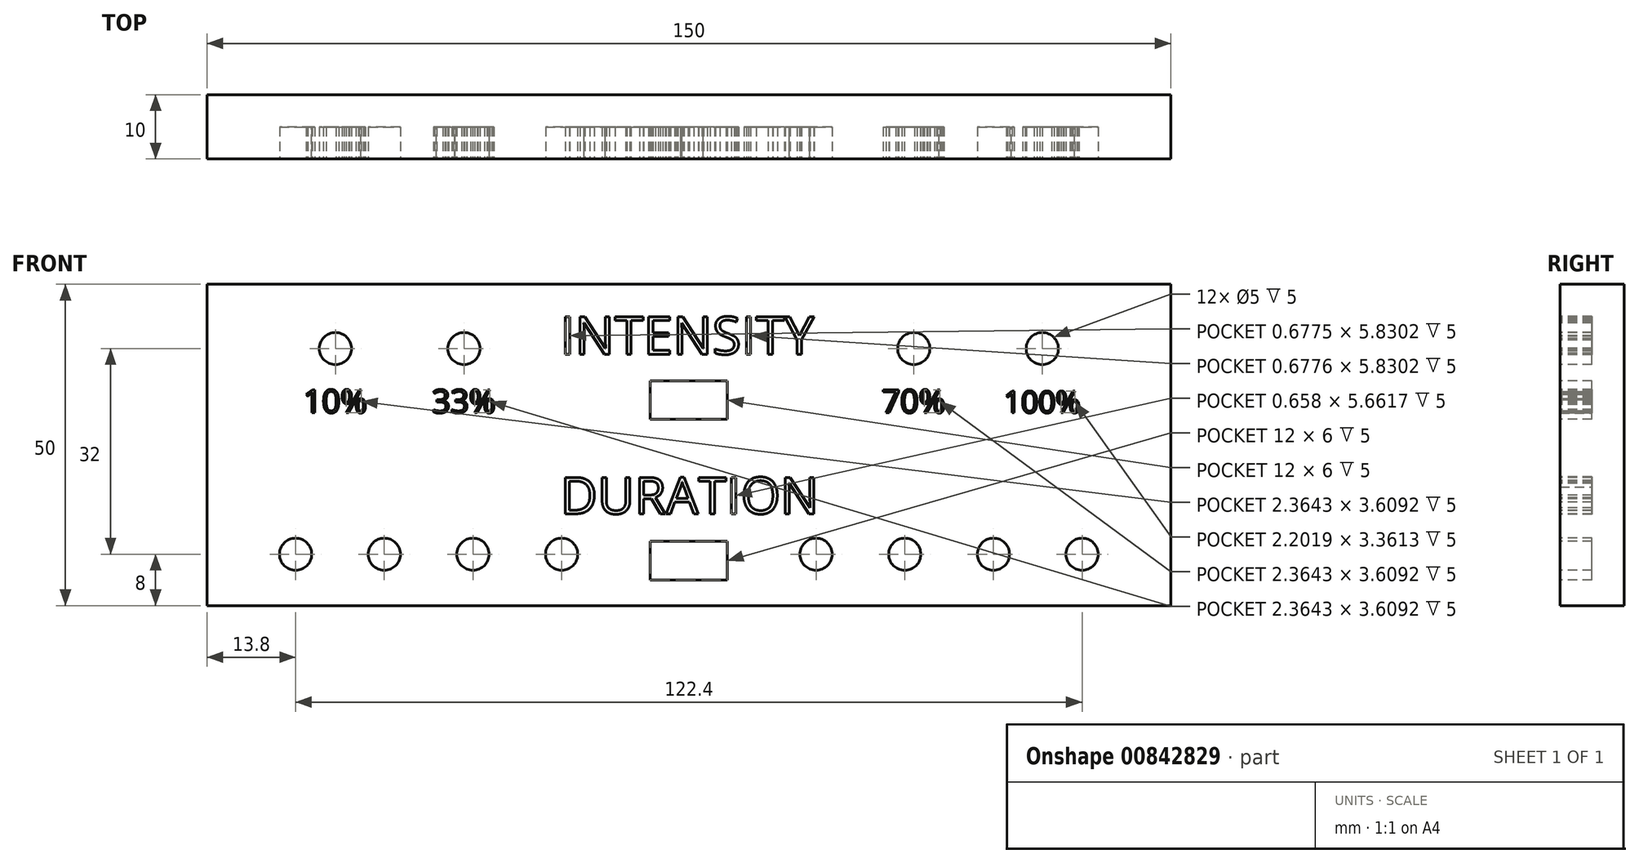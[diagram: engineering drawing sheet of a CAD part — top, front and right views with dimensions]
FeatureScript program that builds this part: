
annotation { "Feature Type Name" : "Feature", "Feature Type Description" : "" }
export const myFeature = defineFeature(function(context is Context, id is Id, definition is map)
    precondition{}
    {
        {
            var Q0;
            Q0=qCreatedBy(makeId("Front.planeOp"),FACE);
            var sketch = newSketch(context, id + "F0", { "sketchPlane" : qUnion([Q0])});
            skLineSegment(sketch, "E0.bottom", {"start": v(75, -25) * mm, "end": v(-75, -25) * mm});
            skLineSegment(sketch, "E0.top", {"start": v(75, 25) * mm, "end": v(-75, 25) * mm});
            skLineSegment(sketch, "E0.left", {"start": v(75, -25) * mm, "end": v(75, 25) * mm});
            skLineSegment(sketch, "E0.right", {"start": v(-75, -25) * mm, "end": v(-75, 25) * mm});
            skPoint(sketch, "E0.middle", {"position": v(0, 0) * mm});
            skSolve(sketch);
        }
        {
            var Q0;
            Q0=makeQuery(id+"F0.imprint","IMPRINT",FACE,{"disambiguationData":[TD([[makeQuery(id+"F0.imprint","IMPRINT",EDGE,{"derivedFrom":sQuery(id+"F0.wireOp",EDGE,"E0.bottom")}),-1.0]])]});
            extrude(context, id + "F1", {"entities" : qUnion([Q0]), "depth" : 10 * mm, "offsetDistance" : 25 * mm});
        }
        {
            var Q0;
            Q0=makeQuery(id+"F1.opExtrude","CAP_FACE",FACE,{"disambiguationData":[OSD([sQuery(id+"F0.wireOp",EDGE,"E0.bottom"),sQuery(id+"F0.wireOp",EDGE,"E0.top"),sQuery(id+"F0.wireOp",EDGE,"E0.left"),sQuery(id+"F0.wireOp",EDGE,"E0.right")])],"isStart":false});
            var sketch = newSketch(context, id + "F2", { "sketchPlane" : qUnion([Q0])});
            skText(sketch, "E1", { "text": "INTENSITY", "fontName": "OpenSans-Regular.ttf"});
            skText(sketch, "E2", { "text": "DURATION", "fontName": "OpenSans-Regular.ttf"});
            const initialGuessF2  = {"E1": [-0.02, 0.01412, 1, 0, 0.00588], "E2": [-0.02, -0.01071, 1, 0, 0.00571]};
            skSetInitialGuess(sketch, initialGuessF2);
            skSolve(sketch);
        }
        {
            var Q0;
            Q0 = qSketchRegion(id + "F2", true);
            extrude(context, id + "F3", {"entities" : qUnion([Q0]), "operationType" : NewBodyOperationType.REMOVE, "oppositeDirection" : true, "depth" : 5 * mm, "offsetDistance" : 25 * mm});
        }
        {
            var Q0;
            {var subQ0=sQuery(id+"F0.wireOp",EDGE,"E0.top");var subQ1=sQuery(id+"F0.wireOp",EDGE,"E0.right");var subQ2=sQuery(id+"F0.wireOp",EDGE,"E0.bottom");var subQ3=sQuery(id+"F0.wireOp",EDGE,"E0.left");Q0=makeQuery(id+"F3.boolean.opBoolean","SPLIT",FACE,{"disambiguationData":[TD([makeQuery(id+"F1.opExtrude","SWEPT_FACE",FACE,{"disambiguationData":[OSD([subQ2])]})])],"derivedFrom":makeQuery(id+"F1.opExtrude","CAP_FACE",FACE,{"disambiguationData":[OSD([subQ2,subQ0,subQ3,subQ1])],"isStart":false})});}
            var sketch = newSketch(context, id + "F4", { "sketchPlane" : qUnion([Q0])});
            skLineSegment(sketch, "E3.bottom", {"start": v(6, 4) * mm, "end": v(-6, 4) * mm});
            skLineSegment(sketch, "E3.top", {"start": v(6, 10) * mm, "end": v(-6, 10) * mm});
            skLineSegment(sketch, "E3.left", {"start": v(6, 4) * mm, "end": v(6, 10) * mm});
            skLineSegment(sketch, "E3.right", {"start": v(-6, 4) * mm, "end": v(-6, 10) * mm});
            skPoint(sketch, "E3.middle", {"position": v(0, 7) * mm});
            skLineSegment(sketch, "E4.bottom", {"start": v(6, -21) * mm, "end": v(-6, -21) * mm});
            skLineSegment(sketch, "E4.top", {"start": v(6, -15) * mm, "end": v(-6, -15) * mm});
            skLineSegment(sketch, "E4.left", {"start": v(6, -21) * mm, "end": v(6, -15) * mm});
            skLineSegment(sketch, "E4.right", {"start": v(-6, -21) * mm, "end": v(-6, -15) * mm});
            skPoint(sketch, "E4.middle", {"position": v(0, -18) * mm});
            skSolve(sketch);
        }
        {
            var Q0;
            Q0 = qSketchRegion(id + "F4", true);
            extrude(context, id + "F5", {"entities" : qUnion([Q0]), "operationType" : NewBodyOperationType.REMOVE, "oppositeDirection" : true, "depth" : 5 * mm, "offsetDistance" : 25 * mm});
        }
        {
            var Q0;
            {var subQ0=sQuery(id+"F0.wireOp",EDGE,"E0.top");var subQ1=sQuery(id+"F0.wireOp",EDGE,"E0.right");var subQ2=sQuery(id+"F0.wireOp",EDGE,"E0.bottom");var subQ3=sQuery(id+"F0.wireOp",EDGE,"E0.left");Q0=makeQuery(id+"F3.boolean.opBoolean","SPLIT",FACE,{"disambiguationData":[TD([makeQuery(id+"F1.opExtrude","SWEPT_FACE",FACE,{"disambiguationData":[OSD([subQ2])]})])],"derivedFrom":makeQuery(id+"F1.opExtrude","CAP_FACE",FACE,{"disambiguationData":[OSD([subQ2,subQ0,subQ3,subQ1])],"isStart":false})});}
            var sketch = newSketch(context, id + "F6", { "sketchPlane" : qUnion([Q0])});
            skCircle(sketch, "E5", {"center": v(-55, 15) * mm, "radius": 2.5 * mm});
            skPoint(sketch, "E6.centerSnap0", {"position": v(12.3, 16.74) * mm});
            skCircle(sketch, "E7", {"center": v(35, 15) * mm, "radius": 2.5 * mm});
            skCircle(sketch, "E8", {"center": v(-35, 15) * mm, "radius": 2.5 * mm});
            skCircle(sketch, "E9", {"center": v(55, 15) * mm, "radius": 2.5 * mm});
            skSolve(sketch);
        }
        {
            var Q0;
            Q0=makeQuery(id+"F6.imprint","IMPRINT",FACE,{"disambiguationData":[TD([[makeQuery(id+"F6.imprint","IMPRINT",EDGE,{"derivedFrom":sQuery(id+"F6.wireOp",EDGE,"E5")}),1.0]])]});
            var Q1;
            Q1=makeQuery(id+"F6.imprint","IMPRINT",FACE,{"disambiguationData":[TD([[makeQuery(id+"F6.imprint","IMPRINT",EDGE,{"derivedFrom":sQuery(id+"F6.wireOp",EDGE,"E8")}),1.0]])]});
            var Q2;
            Q2=makeQuery(id+"F6.imprint","IMPRINT",FACE,{"disambiguationData":[TD([[makeQuery(id+"F6.imprint","IMPRINT",EDGE,{"derivedFrom":sQuery(id+"F6.wireOp",EDGE,"E7")}),1.0]])]});
            var Q3;
            Q3=makeQuery(id+"F6.imprint","IMPRINT",FACE,{"disambiguationData":[TD([[makeQuery(id+"F6.imprint","IMPRINT",EDGE,{"derivedFrom":sQuery(id+"F6.wireOp",EDGE,"E9")}),1.0]])]});
            extrude(context, id + "F7", {"entities" : qUnion([Q0, Q1, Q2, Q3]), "operationType" : NewBodyOperationType.REMOVE, "oppositeDirection" : true, "depth" : 5 * mm, "offsetDistance" : 25 * mm});
        }
        {
            var Q0;
            {var subQ0=sQuery(id+"F0.wireOp",EDGE,"E0.top");var subQ1=sQuery(id+"F0.wireOp",EDGE,"E0.right");var subQ2=sQuery(id+"F0.wireOp",EDGE,"E0.bottom");var subQ3=sQuery(id+"F0.wireOp",EDGE,"E0.left");Q0=makeQuery(id+"F3.boolean.opBoolean","SPLIT",FACE,{"disambiguationData":[TD([makeQuery(id+"F1.opExtrude","SWEPT_FACE",FACE,{"disambiguationData":[OSD([subQ2])]})])],"derivedFrom":makeQuery(id+"F1.opExtrude","CAP_FACE",FACE,{"disambiguationData":[OSD([subQ2,subQ0,subQ3,subQ1])],"isStart":false})});}
            var sketch = newSketch(context, id + "F8", { "sketchPlane" : qUnion([Q0])});
            skText(sketch, "E10", { "text": "33%", "fontName": "OpenSans-Regular.ttf"});
            skText(sketch, "E11", { "text": "70%", "fontName": "OpenSans-Regular.ttf"});
            skText(sketch, "E12", { "text": "100%", "fontName": "OpenSans-Regular.ttf"});
            skText(sketch, "E13", { "text": "10%", "fontName": "OpenSans-Regular.ttf"});
            const initialGuessF8  = {"E10": [-0.04, 0.005, 1, 0, 0.00364], "E11": [0.03, 0.005, 1, 0, 0.00364], "E12": [0.049, 0.005, 1, 0, 0.00339], "E13": [-0.06, 0.005, 1, 0, 0.00364]};
            skSetInitialGuess(sketch, initialGuessF8);
            skSolve(sketch);
        }
        {
            var Q0;
            Q0 = qSketchRegion(id + "F8", true);
            extrude(context, id + "F9", {"entities" : qUnion([Q0]), "operationType" : NewBodyOperationType.REMOVE, "oppositeDirection" : true, "depth" : 5 * mm, "offsetDistance" : 25 * mm});
        }
        {
            var Q0;
            {var subQ98=sQuery(id+"F0.wireOp",EDGE,"E0.bottom");var subQ99=makeQuery(id+"F1.opExtrude","SWEPT_FACE",FACE,{"disambiguationData":[OSD([subQ98])]});var subQ107=sQuery(id+"F0.wireOp",EDGE,"E0.right");var subQ114=sQuery(id+"F0.wireOp",EDGE,"E0.top");var subQ120=sQuery(id+"F0.wireOp",EDGE,"E0.left");Q0=makeQuery(id+"F9.boolean.opBoolean","SPLIT",FACE,{"disambiguationData":[TD([subQ99])],"derivedFrom":makeQuery(id+"F3.boolean.opBoolean","SPLIT",FACE,{"disambiguationData":[TD([subQ99])],"derivedFrom":makeQuery(id+"F1.opExtrude","CAP_FACE",FACE,{"disambiguationData":[OSD([subQ98,subQ114,subQ120,subQ107])],"isStart":false})})});}
            var sketch = newSketch(context, id + "F10", { "sketchPlane" : qUnion([Q0])});
            skCircle(sketch, "E14", {"center": v(-61.2, -17) * mm, "radius": 2.5 * mm});
            skCircle(sketch, "E15", {"center": v(-47.4, -17) * mm, "radius": 2.5 * mm});
            skCircle(sketch, "E16", {"center": v(-33.6, -17) * mm, "radius": 2.5 * mm});
            skCircle(sketch, "E17", {"center": v(-19.8, -17) * mm, "radius": 2.5 * mm});
            skCircle(sketch, "E18", {"center": v(19.8, -17) * mm, "radius": 2.5 * mm});
            skCircle(sketch, "E19", {"center": v(33.6, -17) * mm, "radius": 2.5 * mm});
            skCircle(sketch, "E20", {"center": v(47.4, -17) * mm, "radius": 2.5 * mm});
            skCircle(sketch, "E21", {"center": v(61.2, -17) * mm, "radius": 2.5 * mm});
            skSolve(sketch);
        }
        {
            var Q0;
            Q0 = qSketchRegion(id + "F10", true);
            extrude(context, id + "F11", {"entities" : qUnion([Q0]), "operationType" : NewBodyOperationType.REMOVE, "oppositeDirection" : true, "depth" : 5 * mm, "offsetDistance" : 25 * mm});
        }
    });
